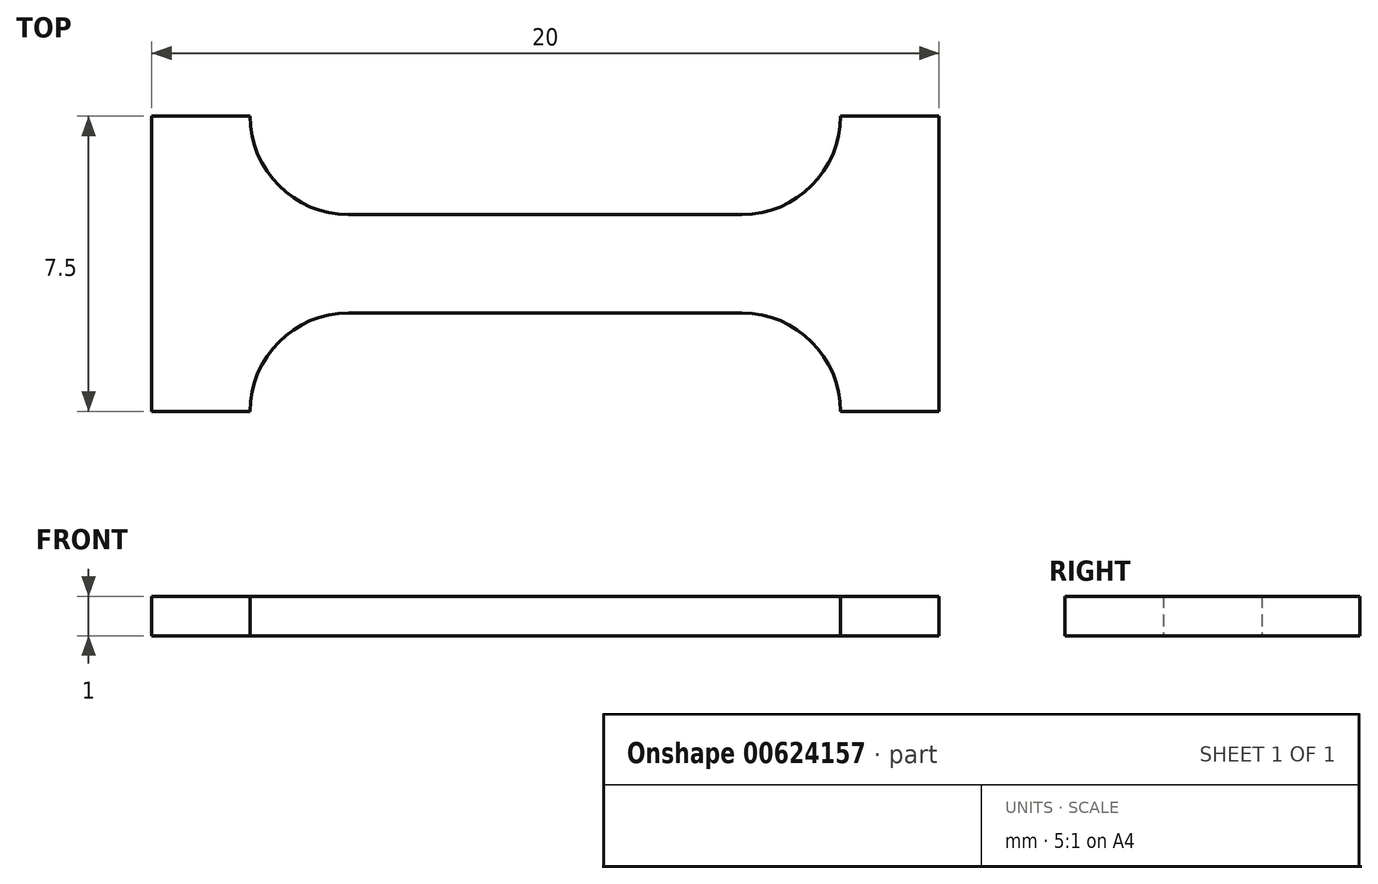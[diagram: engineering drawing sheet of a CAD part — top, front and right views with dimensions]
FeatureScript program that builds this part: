
annotation { "Feature Type Name" : "Feature", "Feature Type Description" : "" }
export const myFeature = defineFeature(function(context is Context, id is Id, definition is map)
    precondition{}
    {
        {
            var Q0;
            Q0=qCreatedBy(makeId("Top.planeOp"),FACE);
            var sketch = newSketch(context, id + "F0", { "sketchPlane" : qUnion([Q0])});
            skLineSegment(sketch, "E0.bottom", {"start": v(5, -1.25) * mm, "end": v(-5, -1.25) * mm, "construction": true});
            skLineSegment(sketch, "E0.top", {"start": v(5, 1.25) * mm, "end": v(-5, 1.25) * mm, "construction": true});
            skLineSegment(sketch, "E0.left", {"start": v(5, -1.25) * mm, "end": v(5, 1.25) * mm, "construction": true});
            skLineSegment(sketch, "E0.right", {"start": v(-5, -1.25) * mm, "end": v(-5, 1.25) * mm, "construction": true});
            skPoint(sketch, "E0.middle", {"position": v(0, 0) * mm});
            skLineSegment(sketch, "E1.bottom", {"start": v(5, 1.25) * mm, "end": v(7.5, 1.25) * mm, "construction": true});
            skLineSegment(sketch, "E1.top", {"start": v(5, -1.25) * mm, "end": v(7.5, -1.25) * mm, "construction": true});
            skLineSegment(sketch, "E1.left", {"start": v(5, 1.25) * mm, "end": v(5, -1.25) * mm, "construction": true});
            skLineSegment(sketch, "E1.right", {"start": v(7.5, 1.25) * mm, "end": v(7.5, -1.25) * mm, "construction": true});
            skLineSegment(sketch, "E2.bottom", {"start": v(7.5, 1.25) * mm, "end": v(10, 1.25) * mm, "construction": true});
            skLineSegment(sketch, "E2.top", {"start": v(7.5, -1.25) * mm, "end": v(10, -1.25) * mm, "construction": true});
            skLineSegment(sketch, "E2.right", {"start": v(10, 1.25) * mm, "end": v(10, -1.25) * mm, "construction": true});
            skLineSegment(sketch, "E3.top", {"start": v(7.5, 3.75) * mm, "end": v(10, 3.75) * mm, "construction": true});
            skLineSegment(sketch, "E3.left", {"start": v(7.5, 1.25) * mm, "end": v(7.5, 3.75) * mm, "construction": true});
            skLineSegment(sketch, "E3.right", {"start": v(10, 1.25) * mm, "end": v(10, 3.75) * mm, "construction": true});
            skLineSegment(sketch, "E4.top", {"start": v(7.5, -3.75) * mm, "end": v(10, -3.75) * mm, "construction": true});
            skLineSegment(sketch, "E4.left", {"start": v(7.5, -1.25) * mm, "end": v(7.5, -3.75) * mm, "construction": true});
            skLineSegment(sketch, "E4.right", {"start": v(10, -1.25) * mm, "end": v(10, -3.75) * mm, "construction": true});
            skLineSegment(sketch, "E5.bottom", {"start": v(7.5, 1.25) * mm, "end": v(5, 1.25) * mm, "construction": true});
            skLineSegment(sketch, "E5.top", {"start": v(7.5, 3.75) * mm, "end": v(5, 3.75) * mm, "construction": true});
            skLineSegment(sketch, "E5.right", {"start": v(5, 1.25) * mm, "end": v(5, 3.75) * mm, "construction": true});
            skArc(sketch, "E6", {"start": v(5, 1.25) * mm, "mid": v(6.77, 1.98) * mm, "end": v(7.5, 3.75) * mm});
            skLineSegment(sketch, "E7.top", {"start": v(5, -3.75) * mm, "end": v(7.5, -3.75) * mm, "construction": true});
            skLineSegment(sketch, "E7.left", {"start": v(5, -1.25) * mm, "end": v(5, -3.75) * mm, "construction": true});
            skArc(sketch, "E8", {"start": v(5, -1.25) * mm, "mid": v(6.77, -1.98) * mm, "end": v(7.5, -3.75) * mm});
            skLineSegment(sketch, "E9", {"start": v(7.5, -3.75) * mm, "end": v(10, -3.75) * mm});
            skLineSegment(sketch, "E10", {"start": v(10, -3.75) * mm, "end": v(10, 3.75) * mm});
            skLineSegment(sketch, "E11", {"start": v(10, 3.75) * mm, "end": v(7.5, 3.75) * mm});
            skLineSegment(sketch, "E12", {"start": v(0, 1.25) * mm, "end": v(0, -1.25) * mm, "construction": true});
            skLineSegment(sketch, "E13", {"start": v(5, 1.25) * mm, "end": v(0, 1.25) * mm});
            skLineSegment(sketch, "E14", {"start": v(0, 1.25) * mm, "end": v(0, -1.25) * mm});
            skLineSegment(sketch, "E15", {"start": v(0, -1.25) * mm, "end": v(5, -1.25) * mm});
            skLineSegment(sketch, "E16.bottom", {"start": v(-5, 1.25) * mm, "end": v(-7.5, 1.25) * mm, "construction": true});
            skLineSegment(sketch, "E16.top", {"start": v(-5, -1.25) * mm, "end": v(-7.5, -1.25) * mm, "construction": true});
            skLineSegment(sketch, "E16.left", {"start": v(-5, 1.25) * mm, "end": v(-5, -1.25) * mm, "construction": true});
            skLineSegment(sketch, "E16.right", {"start": v(-7.5, 1.25) * mm, "end": v(-7.5, -1.25) * mm, "construction": true});
            skLineSegment(sketch, "E17.bottom", {"start": v(-7.5, 1.25) * mm, "end": v(-10, 1.25) * mm, "construction": true});
            skLineSegment(sketch, "E17.top", {"start": v(-7.5, -1.25) * mm, "end": v(-10, -1.25) * mm, "construction": true});
            skLineSegment(sketch, "E17.right", {"start": v(-10, 1.25) * mm, "end": v(-10, -1.25) * mm, "construction": true});
            skLineSegment(sketch, "E18.bottom", {"start": v(-10, 1.25) * mm, "end": v(-7.5, 1.25) * mm, "construction": true});
            skLineSegment(sketch, "E18.top", {"start": v(-10, 3.75) * mm, "end": v(-7.5, 3.75) * mm, "construction": true});
            skLineSegment(sketch, "E18.left", {"start": v(-10, 1.25) * mm, "end": v(-10, 3.75) * mm, "construction": true});
            skLineSegment(sketch, "E18.right", {"start": v(-7.5, 1.25) * mm, "end": v(-7.5, 3.75) * mm, "construction": true});
            skLineSegment(sketch, "E19.bottom", {"start": v(-7.5, 3.75) * mm, "end": v(-5, 3.75) * mm, "construction": true});
            skLineSegment(sketch, "E19.top", {"start": v(-7.5, 1.25) * mm, "end": v(-5, 1.25) * mm, "construction": true});
            skLineSegment(sketch, "E19.left", {"start": v(-7.5, 3.75) * mm, "end": v(-7.5, 1.25) * mm, "construction": true});
            skLineSegment(sketch, "E19.right", {"start": v(-5, 3.75) * mm, "end": v(-5, 1.25) * mm, "construction": true});
            skLineSegment(sketch, "E20.bottom", {"start": v(-7.5, -1.25) * mm, "end": v(-5, -1.25) * mm, "construction": true});
            skLineSegment(sketch, "E20.top", {"start": v(-7.5, -3.75) * mm, "end": v(-5, -3.75) * mm, "construction": true});
            skLineSegment(sketch, "E20.left", {"start": v(-7.5, -1.25) * mm, "end": v(-7.5, -3.75) * mm, "construction": true});
            skLineSegment(sketch, "E20.right", {"start": v(-5, -1.25) * mm, "end": v(-5, -3.75) * mm, "construction": true});
            skLineSegment(sketch, "E21.bottom", {"start": v(-7.5, -3.75) * mm, "end": v(-10, -3.75) * mm, "construction": true});
            skLineSegment(sketch, "E21.left", {"start": v(-7.5, -3.75) * mm, "end": v(-7.5, -1.25) * mm, "construction": true});
            skLineSegment(sketch, "E21.right", {"start": v(-10, -3.75) * mm, "end": v(-10, -1.25) * mm, "construction": true});
            skArc(sketch, "E22", {"start": v(-7.5, 3.75) * mm, "mid": v(-6.77, 1.98) * mm, "end": v(-5, 1.25) * mm});
            skArc(sketch, "E23", {"start": v(-7.5, -3.75) * mm, "mid": v(-6.77, -1.98) * mm, "end": v(-5, -1.25) * mm});
            skLineSegment(sketch, "E24", {"start": v(-7.5, -3.75) * mm, "end": v(-10, -3.75) * mm});
            skLineSegment(sketch, "E25", {"start": v(-10, -3.75) * mm, "end": v(-10, 3.75) * mm});
            skLineSegment(sketch, "E26", {"start": v(-10, 3.75) * mm, "end": v(-7.5, 3.75) * mm});
            skLineSegment(sketch, "E27", {"start": v(-5, 1.25) * mm, "end": v(0, 1.25) * mm});
            skLineSegment(sketch, "E28", {"start": v(-5, -1.25) * mm, "end": v(0, -1.25) * mm});
            skSolve(sketch);
        }
        {
            var Q0;
            Q0=makeQuery(id+"F0.imprint","IMPRINT",FACE,{"disambiguationData":[TD([[makeQuery(id+"F0.imprint","IMPRINT",EDGE,{"derivedFrom":sQuery(id+"F0.wireOp",EDGE,"E14")}),-1.0]])]});
            var Q1;
            Q1=makeQuery(id+"F0.imprint","IMPRINT",FACE,{"disambiguationData":[TD([[makeQuery(id+"F0.imprint","IMPRINT",EDGE,{"derivedFrom":sQuery(id+"F0.wireOp",EDGE,"E6")}),-1.0]])]});
            extrude(context, id + "F1", {"entities" : qUnion([Q0, Q1]), "depth" : 1 * mm, "offsetDistance" : 25 * mm});
        }
    });
